# Revit family: revitupgrade
name_source: partatom
category: Furniture
units: mm (PartAtom-declared; Revit-internal decimal feet)

## family parameters
Always vertical = Yes
Cut with Voids When Loaded = No
Enable Cutting in Views = No
OmniClass Number = 23.40.70.14.64.11
OmniClass Title = Office Furniture
Render Appearance Source = Family Geometry
Room Calculation Point = No
Shared = Yes
Work Plane-Based = No

## types (2) — shared parameters
Assembly Code = E2020200
Default Elevation = 0.00 mm
Description = LexCo Collection is a comprehensive desking platform designed for customisation to enable greater tailored expression and bringing new personality to the workspace.
Manufacturer = Steelcase
Release Date = Febraury 2023
Style Number(s) = FBOSMPDP,FBOSMPDA,FBOSMPDM
URL = https://www.steelcase.com

## per-type parameters (varying)
| type | A Leg | Stance Leg |
| For Stance Leg | No | Yes |
| For A Leg | Yes | No |

## geometry (parser evidence)
native form markers: Sweep x2
no freeform markers — native parametric forms only
